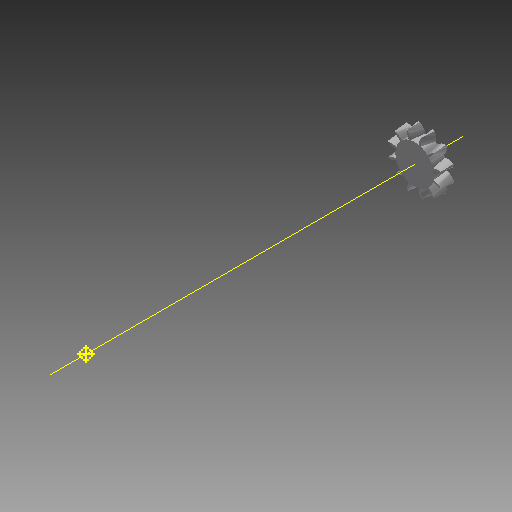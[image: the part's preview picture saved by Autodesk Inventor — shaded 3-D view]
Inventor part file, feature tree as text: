
AUTODESK INVENTOR PART (.ipt)
format: ipt  version: 2017 (Build 210142000, 142)  size: 449,024 bytes
history: native  units: mm
features: other x24, loft x2, pattern_circular x2, sketch x1
ambient origin geometry x6: Origin, XZ Plane, X Axis, Y Axis, Z Axis, Center Point
bodies: Solid1 (feature_tree)
feature tree (29):
  other  "Top Point"
  other  "Mesh Plane2"
  other  "Teeth Body"
  other  "Start Point"
  other  "Tooth Plane"
  other  "Start Sketch"
  other  "End Point"
  other  "3D Sketch Right"
  other  "End Plane Right"
  loft  "Loft Right"
  pattern_circular  "Circular Pattern Right"  [2 undecoded]
  other  "3D Sketch Left"
  other  "End Plane Left"
  loft  "Loft Left"
  pattern_circular  "Circular Pattern Left"  [2 undecoded]
  other  "Fix Body"
  other  "Mesh Plane"
  other  "Top Plane"
  other  "Teeth Body Sketch"
  other  "End Plane"
  other  "End Sketch"
  other  "Helical Curve Left"
  other  "End Sketch Left"
  other  "Body Sketch"
  sketch  "Sketch6"  dims[d0=20.32mm d1=16.688585mm d2=23.784577mm d3=5.08mm d4=142.116265mm d5=90.0deg d7=5.002377mm d8=5.46723mm d9=7.462502mm d11=5.257852mm d17=0.0mm d18=90.0deg d19=0.0mm d20=90.0deg d21=120.0mm d22=360.0deg d26=126.354885mm d27=5.24449mm d28=20.32mm d29=-0.713075mm d30=4.822938mm d31=5.271117mm d32=7.194817mm d35=0.0mm d37=0.0mm d39=0.0mm d40=90.0deg d41=120.0mm d42=360.0deg d46=90.0deg d47=90.0deg d48=0.0mm d49=0.0mm d50=90.0deg d51=15.0deg d52=0.0mm d53=0.0mm d54=0.0mm d56=11.439508mm d57=12.989698mm d58=7.938708mm d59=12.523748mm d60=7.653941mm d61=12.523748mm d62=7.653941mm d63=90.0deg d64=90.0deg d65=126.354885mm d66=31.5mm d67=20.32mm d68=-0.713075mm d69=5.24449mm d70=5.271117mm d71=7.194817mm d72=4.822938mm d73=7.653941mm d74=12.523748mm d75=0.0mm d76=90.0deg d77=0.0mm d78=90.0deg d79=0.0mm d80=90.0deg d81=120.0mm d82=360.0deg d84=10.0mm d85=20.0mm d86=20.0mm d87=10.0mm d88=0.0mm d89=0.0mm d90=0.635mm]
  other  "Srf1"
  other  "Helical Curve Right"
  other  "End Sketch Right"
  other  "Pitch Diameter"
note: 4 required parameter values undecoded (feature->parameter linkage not recoverable at this tier; creation-order binding heuristic only, values carry confidence <= 0.55)
